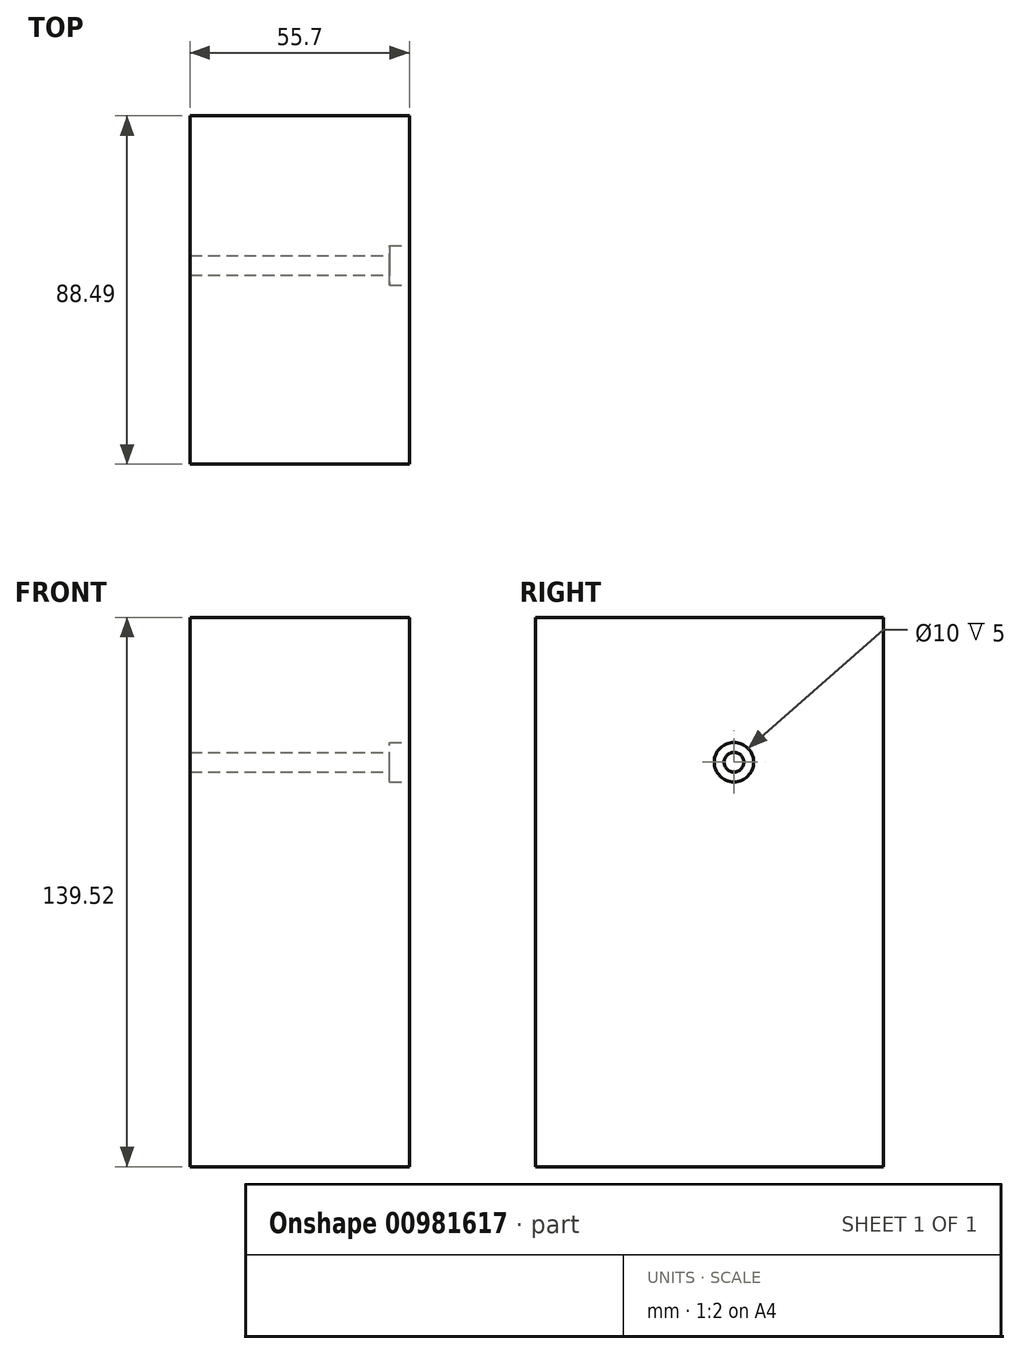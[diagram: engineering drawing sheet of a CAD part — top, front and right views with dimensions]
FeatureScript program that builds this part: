
annotation { "Feature Type Name" : "Feature", "Feature Type Description" : "" }
export const myFeature = defineFeature(function(context is Context, id is Id, definition is map)
    precondition{}
    {
        {
            var Q0;
            Q0=qCreatedBy(makeId("Right.planeOp"),FACE);
            var sketch = newSketch(context, id + "F0", { "sketchPlane" : qUnion([Q0])});
            skLineSegment(sketch, "E0.bottom", {"start": v(53.22, 94.68) * mm, "end": v(-35.27, 94.68) * mm});
            skLineSegment(sketch, "E0.top", {"start": v(53.22, -22.55) * mm, "end": v(-35.27, -22.55) * mm});
            skLineSegment(sketch, "E0.left", {"start": v(53.22, 94.68) * mm, "end": v(53.22, -22.55) * mm});
            skLineSegment(sketch, "E0.right", {"start": v(-35.27, 94.68) * mm, "end": v(-35.27, -22.55) * mm});
            skSolve(sketch);
        }
        {
            var Q0;
            Q0=makeQuery(id+"F0.imprint","IMPRINT",FACE,{"disambiguationData":[TD([[makeQuery(id+"F0.imprint","IMPRINT",EDGE,{"derivedFrom":sQuery(id+"F0.wireOp",EDGE,"E0.bottom")}),1.0]])]});
            extrude(context, id + "F1", {"entities" : qUnion([Q0]), "endBound" : BoundingType.SYMMETRIC, "oppositeDirection" : true, "depth" : 55.7 * mm, "offsetDistance" : 25 * mm});
        }
        {
            var Q0;
            Q0=makeQuery(id+"F1.opExtrude","SWEPT_FACE",FACE,{"disambiguationData":[OSD([sQuery(id+"F0.wireOp",EDGE,"E0.bottom")])]});
            extrude(context, id + "F2", {"entities" : qUnion([Q0]), "operationType" : NewBodyOperationType.ADD, "depth" : 22.29 * mm, "offsetDistance" : 25 * mm});
        }
        {
            var Q0;
            {var subQ0=sQuery(id+"F0.wireOp",EDGE,"E0.bottom");Q0=makeQuery(id+"F2.boolean.opBoolean","MERGE",FACE,{"derivedFrom":[makeQuery(id+"F1.opExtrude","CAP_FACE",FACE,{"disambiguationData":[OSD([subQ0,sQuery(id+"F0.wireOp",EDGE,"E0.top"),sQuery(id+"F0.wireOp",EDGE,"E0.left"),sQuery(id+"F0.wireOp",EDGE,"E0.right")])],"isStart":true}),makeQuery(id+"F2.opExtrude","SWEPT_FACE",FACE,{"disambiguationData":[OSD([subQ0]),TDD([makeQuery(id+"F1.opExtrude","CAP_EDGE",EDGE,{"disambiguationData":[OSD([subQ0])],"isStart":true})])]})]});}
            var sketch = newSketch(context, id + "F3", { "sketchPlane" : qUnion([Q0])});
            skPoint(sketch, "E1", {"position": v(15.2, 80.22) * mm});
            skSolve(sketch);
        }
        {
            var Q0;
            Q0=sQuery(id+"F3.wireOp",VERTEX,"E1");
            var Q1;
            Q1=makeQuery(id+"F1.opExtrude","SWEPT_BODY",BODY,{"disambiguationData":[OSD([sQuery(id+"F0.wireOp",EDGE,"E0.bottom"),sQuery(id+"F0.wireOp",EDGE,"E0.top"),sQuery(id+"F0.wireOp",EDGE,"E0.left"),sQuery(id+"F0.wireOp",EDGE,"E0.right")])]});
            hole(context, id + "F4", {"style" : HoleStyle.C_BORE, "endStyle" : HoleEndStyle.THROUGH, "holeDiameter" : 5 * mm, "cBoreDiameter" : 10 * mm, "cBoreDepth" : 5 * mm, "majorDiameter" : 5 * mm, "isTappedThrough" : true, "tappedDepth" : 12 * mm, "tapClearance" : 3, "locations" : qUnion([Q0]), "scope" : qUnion([Q1])});
        }
    });
